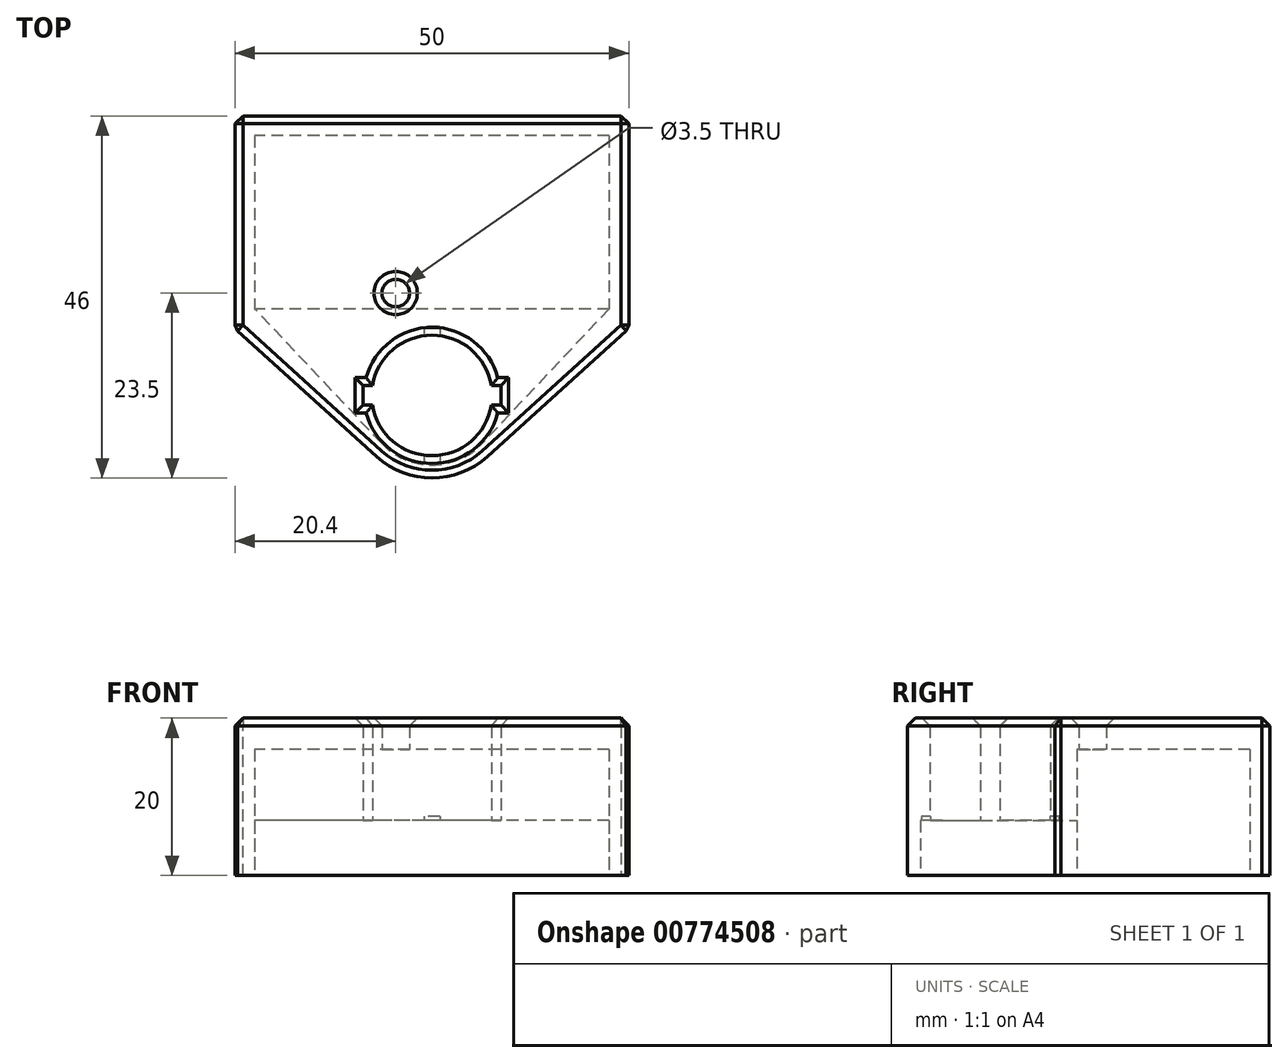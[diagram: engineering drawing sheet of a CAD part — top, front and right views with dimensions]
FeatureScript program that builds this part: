
annotation { "Feature Type Name" : "Feature", "Feature Type Description" : "" }
export const myFeature = defineFeature(function(context is Context, id is Id, definition is map)
    precondition{}
    {
        {
            var Q0;
            Q0=qCreatedBy(makeId("Top.planeOp"),FACE);
            var sketch = newSketch(context, id + "F0", { "sketchPlane" : qUnion([Q0])});
            skLineSegment(sketch, "E0.top", {"start": v(25, 13.5) * mm, "end": v(-25, 13.5) * mm});
            skLineSegment(sketch, "E0.left", {"start": v(25, -13.5) * mm, "end": v(25, 13.5) * mm});
            skLineSegment(sketch, "E0.right", {"start": v(-25, -13.5) * mm, "end": v(-25, 13.5) * mm});
            skPoint(sketch, "E0.middle", {"position": v(0, 0) * mm});
            skArc(sketch, "E1", {"start": v(-7.05, -29.78) * mm, "mid": v(0, -32.5) * mm, "end": v(7.05, -29.78) * mm});
            skLineSegment(sketch, "E2", {"start": v(-25, -13.5) * mm, "end": v(-7.05, -29.78) * mm});
            skLineSegment(sketch, "E3", {"start": v(25, -13.5) * mm, "end": v(7.05, -29.78) * mm});
            skSolve(sketch);
        }
        {
            var Q0;
            Q0 = qSketchRegion(id + "F0", true);
            extrude(context, id + "F1", {"entities" : qUnion([Q0]), "depth" : 20 * mm, "offsetDistance" : 25 * mm});
        }
        {
            var Q0;
            Q0=makeQuery(id+"F1.opExtrude","CAP_FACE",FACE,{"disambiguationData":[OSD([sQuery(id+"F0.wireOp",EDGE,"E0.top"),sQuery(id+"F0.wireOp",EDGE,"E0.left"),sQuery(id+"F0.wireOp",EDGE,"E0.right"),sQuery(id+"F0.wireOp",EDGE,"E1"),sQuery(id+"F0.wireOp",EDGE,"E2"),sQuery(id+"F0.wireOp",EDGE,"E3")])],"isStart":true});
            var sketch = newSketch(context, id + "F2", { "sketchPlane" : qUnion([Q0])});
            skLineSegment(sketch, "E4.bottom", {"start": v(22.5, -11) * mm, "end": v(-22.5, -11) * mm});
            skLineSegment(sketch, "E4.top", {"start": v(22.5, 11) * mm, "end": v(-22.5, 11) * mm});
            skLineSegment(sketch, "E4.left", {"start": v(22.5, -11) * mm, "end": v(22.5, 11) * mm});
            skLineSegment(sketch, "E4.right", {"start": v(-22.5, -11) * mm, "end": v(-22.5, 11) * mm});
            skPoint(sketch, "E4.middle", {"position": v(0, 0) * mm});
            skSolve(sketch);
        }
        {
            var Q0;
            Q0 = qSketchRegion(id + "F2", true);
            extrude(context, id + "F3", {"entities" : qUnion([Q0]), "operationType" : NewBodyOperationType.REMOVE, "oppositeDirection" : true, "depth" : 16 * mm, "offsetDistance" : 25 * mm});
        }
        {
            var Q0;
            Q0=makeQuery(id+"F1.opExtrude","CAP_FACE",FACE,{"disambiguationData":[OSD([sQuery(id+"F0.wireOp",EDGE,"E0.top"),sQuery(id+"F0.wireOp",EDGE,"E0.left"),sQuery(id+"F0.wireOp",EDGE,"E0.right"),sQuery(id+"F0.wireOp",EDGE,"E1"),sQuery(id+"F0.wireOp",EDGE,"E2"),sQuery(id+"F0.wireOp",EDGE,"E3")])],"isStart":true});
            var sketch = newSketch(context, id + "F4", { "sketchPlane" : qUnion([Q0])});
            skArc(sketch, "E5", {"start": v(7.55, 23.25) * mm, "mid": v(0, 29.65) * mm, "end": v(-7.55, 23.25) * mm});
            skLineSegment(sketch, "E6.bottom", {"start": v(8.75, 20.75) * mm, "end": v(7.55, 20.75) * mm});
            skLineSegment(sketch, "E6.top", {"start": v(8.75, 23.25) * mm, "end": v(7.55, 23.25) * mm});
            skLineSegment(sketch, "E6.left", {"start": v(8.75, 20.75) * mm, "end": v(8.75, 23.25) * mm});
            skLineSegment(sketch, "E6.right", {"start": v(-8.75, 20.75) * mm, "end": v(-8.75, 23.25) * mm});
            skLineSegment(sketch, "E7.trimOffspring", {"start": v(-7.55, 23.25) * mm, "end": v(-8.75, 23.25) * mm});
            skLineSegment(sketch, "E8.trimOffspring", {"start": v(-7.55, 20.75) * mm, "end": v(-8.75, 20.75) * mm});
            skArc(sketch, "E9.trimOffspring", {"start": v(-7.55, 20.75) * mm, "mid": v(0, 14.35) * mm, "end": v(7.55, 20.75) * mm});
            skSolve(sketch);
        }
        {
            var Q0;
            Q0 = qSketchRegion(id + "F4", true);
            extrude(context, id + "F5", {"entities" : qUnion([Q0]), "operationType" : NewBodyOperationType.REMOVE, "endBound" : BoundingType.THROUGH_ALL, "oppositeDirection" : true, "depth" : 25 * mm, "offsetDistance" : 25 * mm});
        }
        {
            var Q0;
            Q0=makeQuery(id+"F1.opExtrude","CAP_FACE",FACE,{"disambiguationData":[OSD([sQuery(id+"F0.wireOp",EDGE,"E0.top"),sQuery(id+"F0.wireOp",EDGE,"E0.left"),sQuery(id+"F0.wireOp",EDGE,"E0.right"),sQuery(id+"F0.wireOp",EDGE,"E1"),sQuery(id+"F0.wireOp",EDGE,"E2"),sQuery(id+"F0.wireOp",EDGE,"E3")])],"isStart":true});
            var sketch = newSketch(context, id + "F6", { "sketchPlane" : qUnion([Q0])});
            skArc(sketch, "E10", {"start": v(6.43, 28.06) * mm, "mid": v(0, 30.84) * mm, "end": v(-6.43, 28.06) * mm});
            skLineSegment(sketch, "E11", {"start": v(-6.43, 28.06) * mm, "end": v(-22.5, 11) * mm});
            skLineSegment(sketch, "E12", {"start": v(-22.5, 11) * mm, "end": v(22.5, 11) * mm});
            skLineSegment(sketch, "E13", {"start": v(22.5, 11) * mm, "end": v(6.43, 28.06) * mm});
            skSolve(sketch);
        }
        {
            var Q0;
            Q0 = qSketchRegion(id + "F6", true);
            extrude(context, id + "F7", {"entities" : qUnion([Q0]), "operationType" : NewBodyOperationType.REMOVE, "oppositeDirection" : true, "depth" : 7 * mm, "offsetDistance" : 25 * mm});
        }
        {
            var Q0;
            {var subQ0=sQuery(id+"F6.wireOp",EDGE,"E10");var subQ1=makeQuery(id+"F7.opExtrude","CAP_FACE",FACE,{"disambiguationData":[OSD([subQ0])],"isStart":false});Q0=makeQuery(id+"F7.boolean.opBoolean","COPY",FACE,{"disambiguationData":[TD([makeQuery(id+"F5.boolean.opBoolean","COPY",FACE,{"derivedFrom":makeQuery(id+"F5.opExtrude","SWEPT_FACE",FACE,{"disambiguationData":[OSD([sQuery(id+"F4.wireOp",EDGE,"E6.bottom")])]})}),makeQuery(id+"F5.boolean.opBoolean","COPY",FACE,{"derivedFrom":makeQuery(id+"F5.opExtrude","SWEPT_FACE",FACE,{"disambiguationData":[OSD([sQuery(id+"F4.wireOp",EDGE,"E6.left")])]})}),makeQuery(id+"F5.boolean.opBoolean","COPY",FACE,{"derivedFrom":makeQuery(id+"F5.opExtrude","SWEPT_FACE",FACE,{"disambiguationData":[OSD([sQuery(id+"F4.wireOp",EDGE,"E6.right")])]})}),makeQuery(id+"F5.boolean.opBoolean","COPY",FACE,{"derivedFrom":makeQuery(id+"F5.opExtrude","SWEPT_FACE",FACE,{"disambiguationData":[OSD([sQuery(id+"F4.wireOp",EDGE,"E8.trimOffspring")])]})}),makeQuery(id+"F5.boolean.opBoolean","COPY",FACE,{"derivedFrom":makeQuery(id+"F5.opExtrude","SWEPT_FACE",FACE,{"disambiguationData":[OSD([sQuery(id+"F4.wireOp",EDGE,"E9.trimOffspring")])]})}),makeQuery(id+"F7.opExtrude","SWEPT_FACE",FACE,{"disambiguationData":[OSD([subQ0])]}),subQ1])],"derivedFrom":subQ1});}
            var sketch = newSketch(context, id + "F8", { "sketchPlane" : qUnion([Q0])});
            skLineSegment(sketch, "E14.bottom", {"start": v(1, 13.25) * mm, "end": v(-1, 13.25) * mm});
            skLineSegment(sketch, "E14.top", {"start": v(1, 30.75) * mm, "end": v(-1, 30.75) * mm});
            skLineSegment(sketch, "E14.left", {"start": v(1, 13.25) * mm, "end": v(1, 30.75) * mm});
            skLineSegment(sketch, "E14.right", {"start": v(-1, 13.25) * mm, "end": v(-1, 30.75) * mm});
            skPoint(sketch, "E14.middle", {"position": v(0, 22) * mm});
            skSolve(sketch);
        }
        {
            var Q0;
            Q0 = qSketchRegion(id + "F8", true);
            extrude(context, id + "F9", {"entities" : qUnion([Q0]), "operationType" : NewBodyOperationType.REMOVE, "oppositeDirection" : true, "depth" : .5 * mm, "offsetDistance" : 25 * mm});
        }
        {
            var Q0;
            Q0=makeQuery(id+"F3.boolean.opBoolean","COPY",FACE,{"derivedFrom":makeQuery(id+"F3.opExtrude","CAP_FACE",FACE,{"disambiguationData":[OSD([sQuery(id+"F2.wireOp",EDGE,"E4.bottom"),sQuery(id+"F2.wireOp",EDGE,"E4.top"),sQuery(id+"F2.wireOp",EDGE,"E4.left"),sQuery(id+"F2.wireOp",EDGE,"E4.right")])],"isStart":false})});
            var sketch = newSketch(context, id + "F10", { "sketchPlane" : qUnion([Q0])});
            skCircle(sketch, "E15", {"center": v(-4.6, 9) * mm, "radius": 1.75 * mm});
            skSolve(sketch);
        }
        {
            var Q0;
            Q0 = qSketchRegion(id + "F10", true);
            extrude(context, id + "F11", {"entities" : qUnion([Q0]), "operationType" : NewBodyOperationType.REMOVE, "endBound" : BoundingType.THROUGH_ALL, "oppositeDirection" : true, "depth" : 25 * mm, "offsetDistance" : 25 * mm});
        }
        {
            var Q0;
            Q0=makeQuery(id+"F1.opExtrude","CAP_FACE",FACE,{"disambiguationData":[OSD([sQuery(id+"F0.wireOp",EDGE,"E0.top"),sQuery(id+"F0.wireOp",EDGE,"E0.left"),sQuery(id+"F0.wireOp",EDGE,"E0.right"),sQuery(id+"F0.wireOp",EDGE,"E1"),sQuery(id+"F0.wireOp",EDGE,"E2"),sQuery(id+"F0.wireOp",EDGE,"E3")])],"isStart":false});
            var Q1;
            Q1=makeQuery(id+"F1.opExtrude","SWEPT_EDGE",EDGE,{"disambiguationData":[OSD([sQuery(id+"F0.wireOp",EDGE,"E0.top"),sQuery(id+"F0.wireOp",EDGE,"E0.right")])]});
            var Q2;
            Q2=makeQuery(id+"F1.opExtrude","SWEPT_EDGE",EDGE,{"disambiguationData":[OSD([sQuery(id+"F0.wireOp",EDGE,"E0.top"),sQuery(id+"F0.wireOp",EDGE,"E0.left")])]});
            var Q3;
            Q3=makeQuery(id+"F1.opExtrude","SWEPT_EDGE",EDGE,{"disambiguationData":[OSD([sQuery(id+"F0.wireOp",EDGE,"E0.left"),sQuery(id+"F0.wireOp",EDGE,"E3")])]});
            var Q4;
            Q4=makeQuery(id+"F1.opExtrude","SWEPT_EDGE",EDGE,{"disambiguationData":[OSD([sQuery(id+"F0.wireOp",EDGE,"E0.right"),sQuery(id+"F0.wireOp",EDGE,"E2")])]});
            chamfer(context, id + "F12", {"entities" : qUnion([Q0, Q1, Q2, Q3, Q4]), "width" : 1 * mm, "tangentPropagation" : true});
        }
    });
